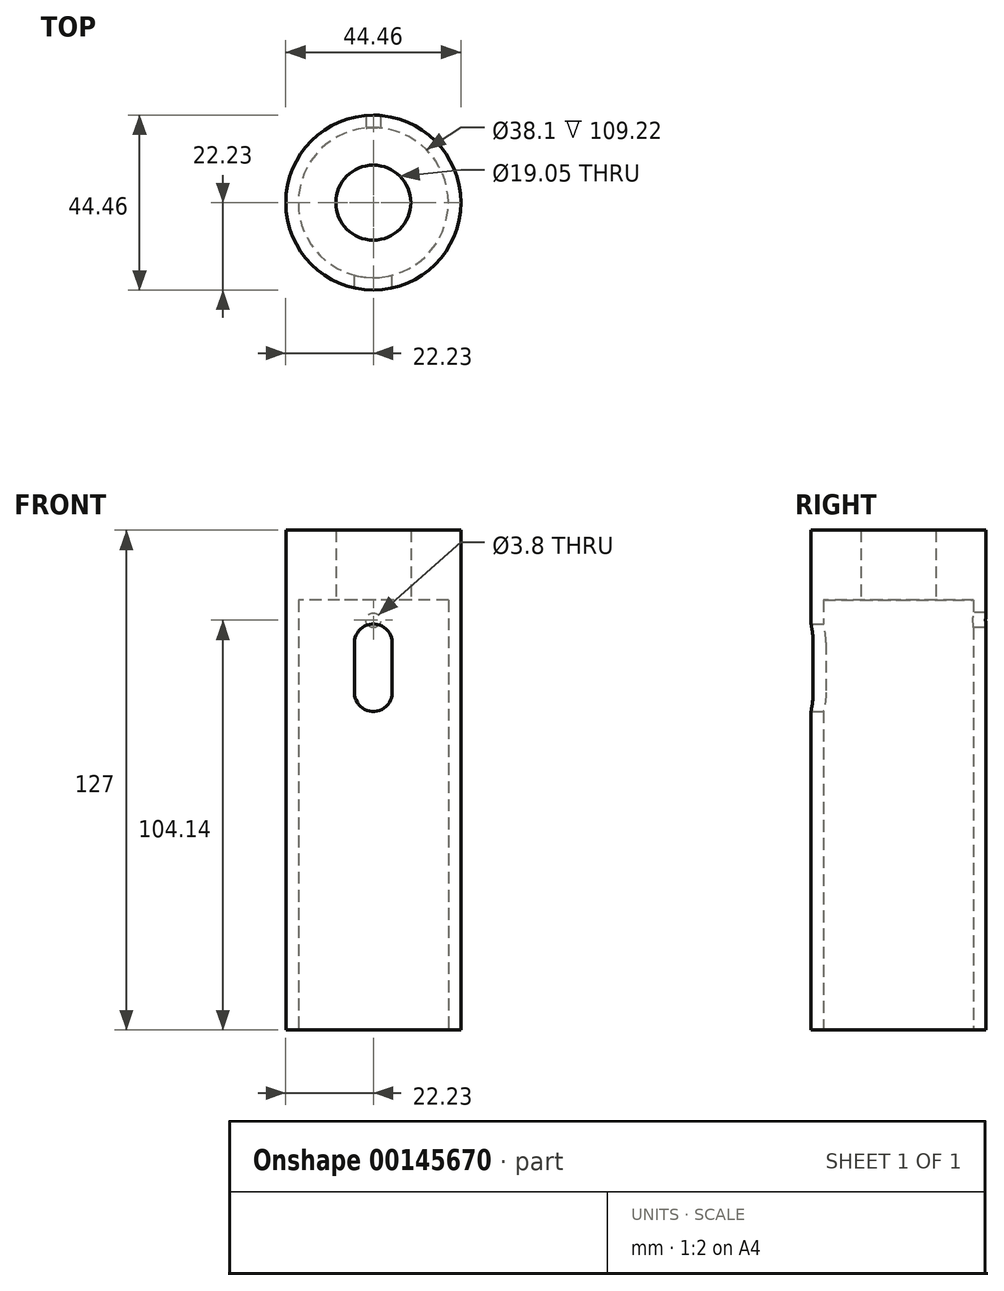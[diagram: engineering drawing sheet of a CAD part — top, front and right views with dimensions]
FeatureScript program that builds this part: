
annotation { "Feature Type Name" : "Feature", "Feature Type Description" : "" }
export const myFeature = defineFeature(function(context is Context, id is Id, definition is map)
    precondition{}
    {
        {
            var Q0;
            Q0=qCreatedBy(makeId("Top.planeOp"),FACE);
            var sketch = newSketch(context, id + "F0", { "sketchPlane" : qUnion([Q0])});
            skCircle(sketch, "E0", {"center": v(0, 0) * mm, "radius": 22.22 * mm});
            skSolve(sketch);
        }
        {
            var Q0;
            Q0=makeQuery(id+"F0.imprint","IMPRINT",FACE,{"disambiguationData":[TD([[makeQuery(id+"F0.imprint","IMPRINT",EDGE,{"derivedFrom":sQuery(id+"F0.wireOp",EDGE,"E0")}),1.0]])]});
            extrude(context, id + "F1", {"entities" : qUnion([Q0]), "depth" : 127 * mm});
        }
        {
            var Q0;
            Q0=qCreatedBy(makeId("Top.planeOp"),FACE);
            var sketch = newSketch(context, id + "F2", { "sketchPlane" : qUnion([Q0])});
            skCircle(sketch, "E1", {"center": v(0, 0) * mm, "radius": 19.05 * mm});
            skSolve(sketch);
        }
        {
            var Q0;
            Q0=makeQuery(id+"F2.imprint","IMPRINT",FACE,{"disambiguationData":[TD([[makeQuery(id+"F2.imprint","IMPRINT",EDGE,{"derivedFrom":sQuery(id+"F2.wireOp",EDGE,"E1")}),1.0]])]});
            extrude(context, id + "F3", {"entities" : qUnion([Q0]), "operationType" : NewBodyOperationType.REMOVE, "depth" : 109.22 * mm});
        }
        {
            var Q0;
            Q0=qCreatedBy(makeId("Top.planeOp"),FACE);
            var sketch = newSketch(context, id + "F4", { "sketchPlane" : qUnion([Q0])});
            skCircle(sketch, "E2", {"center": v(0, 0) * mm, "radius": 9.53 * mm});
            skSolve(sketch);
        }
        {
            var Q0;
            Q0 = qSketchRegion(id + "F4", true);
            extrude(context, id + "F5", {"entities" : qUnion([Q0]), "operationType" : NewBodyOperationType.REMOVE, "endBound" : BoundingType.THROUGH_ALL, "depth" : 25.4 * mm});
        }
        {
            var Q0;
            Q0=qCreatedBy(makeId("Front.planeOp"),FACE);
            var sketch = newSketch(context, id + "F6", { "sketchPlane" : qUnion([Q0])});
            skLineSegment(sketch, "E3.bottom", {"start": v(-4.76, 98.43) * mm, "end": v(4.76, 98.43) * mm});
            skLineSegment(sketch, "E3.top", {"start": v(-4.76, 85.73) * mm, "end": v(4.76, 85.73) * mm});
            skLineSegment(sketch, "E3.left", {"start": v(-4.76, 98.43) * mm, "end": v(-4.76, 85.73) * mm});
            skLineSegment(sketch, "E3.right", {"start": v(4.76, 98.43) * mm, "end": v(4.76, 85.73) * mm});
            skCircle(sketch, "E4", {"center": v(0, 98.43) * mm, "radius": 4.76 * mm});
            skCircle(sketch, "E5", {"center": v(0, 85.73) * mm, "radius": 4.76 * mm});
            skSolve(sketch);
        }
        {
            var Q0;
            Q0 = qSketchRegion(id + "F6", true);
            extrude(context, id + "F7", {"entities" : qUnion([Q0]), "operationType" : NewBodyOperationType.REMOVE, "depth" : 25.4 * mm});
        }
        {
            var Q0;
            Q0=qCreatedBy(makeId("Front.planeOp"),FACE);
            var sketch = newSketch(context, id + "F8", { "sketchPlane" : qUnion([Q0])});
            skPoint(sketch, "E6", {"position": v(0, 104.14) * mm});
            skSolve(sketch);
        }
        {
            var Q0;
            Q0=sQuery(id+"F8.wireOp",VERTEX,"E6");
            var Q1;
            Q1=makeQuery(id+"F1.opExtrude","SWEPT_BODY",BODY,{"disambiguationData":[OSD([sQuery(id+"F0.wireOp",EDGE,"E0")])]});
            hole(context, id + "F9", {"style" : HoleStyle.SIMPLE, "endStyle" : HoleEndStyle.BLIND, "standardTappedOrClearance" : lookupTablePath({ "standard" : "ANSI", "engagement" : "75%", "pitch" : "24 tpi", "size" : "#10", "type" : "Tapped" }), "standardBlindInLast" : lookupTablePath({ "standard" : "ANSI", "engagement" : "75%", "pitch" : "24 tpi", "size" : "#10", "type" : "Tapped" }), "holeDiameter" : 3.8 * mm, "holeDepth" : 12.7 * mm, "locations" : qUnion([Q0]), "scope" : qUnion([Q1]), "majorDiameter" : 4.83 * mm});
        }
    });
